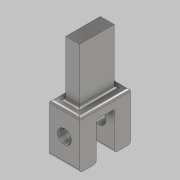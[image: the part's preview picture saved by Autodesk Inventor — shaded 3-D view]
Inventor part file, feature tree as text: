
AUTODESK INVENTOR PART (.ipt)
format: ipt  version: 2021 (Build 250183000, 183)  size: 144,896 bytes
history: native  units: mm
features: sketch x4, extrude x3, fillet x1, hole x1
ambient origin geometry x8: Origin, YZ Plane, XZ Plane, XY Plane, X Axis, Y Axis, Z Axis, Center Point
bodies: Solid1 (feature_tree)
feature tree (9):
  extrude  "sandwich_plate"  Depth=40.0mm
  extrude  "clamp_length"  Depth=12.5mm
  extrude  "slot"  Depth=35.0mm TaperAngle=0.0deg
  fillet  "Fillet1"  Radius=6.0mm
  hole  "Hole1"  [1 undecoded]
  sketch  "Sketch1"  dims[d0=25.0mm d1=40.0mm]
  sketch  "Sketch2"  dims[d2=20.0mm d3=12.5mm]
  sketch  "Sketch3"  dims[d4=10.0mm d5=0.0mm d7=35.0mm d8=0.0mm d9=6.0mm]
  sketch  "Sketch4"  dims[d10=6.0mm d11=6.0mm d12=6.0mm d14=7.5mm d15=12.0mm d16=12.0mm d17=0.0mm d18=0.0mm d19=2.0mm d20=11.0mm d21=17.5mm d22=10.0mm d23=6.0mm d24=4.0mm d25=2.0mm d26=90.0deg d27=8.0mm d28=20.594885mm d6=0.5mm]
note: 1 required parameter value undecoded (feature->parameter linkage not recoverable at this tier; creation-order binding heuristic only, values carry confidence <= 0.55)
